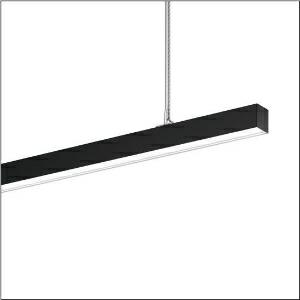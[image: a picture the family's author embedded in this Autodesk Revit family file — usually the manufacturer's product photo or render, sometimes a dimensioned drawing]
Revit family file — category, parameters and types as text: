
# Revit family: silica_21_51mx33dc3dbb
name_source: partatom
category: Lighting Fixtures
units: mm (PartAtom-declared; Revit-internal decimal feet)

## family parameters
Cut with Voids When Loaded = No
Host = Face
Light Source = No
Part Type = Normal
Room Calculation Point = No
Round Connector Dimension = Use Diameter
Shared = No

## types (1)
- --- (1 x LED, 14780 lm, 99.5 W, 3000K)
    Apparent Load = 100 VA
    CIE Flux Codes = 78 96 99 55 100
    Color Rendering = 80
    Color Temperature = 3000K
    Default Elevation = 1800 mm
    Description = Silica 21, office luminaire, primary optical cover: prismatic diffuser, of PMMA, CAT 2 (L<= 3000cd/m²), light emission: direct/indirect distribution, primary light characteristic: symmetric, installation type: suspended mounting, LED, rated luminous flux: 14.780lm, luminous efficacy: 149lm/W, light colour: 830, colour temperature: 3000K, control gear: DALI 2, with terminal, 3+2-pole, max. 2.5mm², mains connection: 220..240V, AC, 50/60Hz, rated input power: 99.5W, luminaire housing, of aluminium, matt jet black (RAL 9005), length: 3.004mm, width: 53mm, height: 53mm, protection rating (complete): IP20, insulation class (complete): insulation class I (protective earthing), certification: CE, permissible operating ambient temperature: 0..+35°C, standard: EN 50419, packaging unit: 1 piece
    Height = 53 mm
    Lamp = 1 x LED
    Lamp Light Flux = 14780 lm
    Lamp Power = 99.5 W
    Lamp count = 1
    Length = 3004 mm
    Luminous efficacy = 149 lm/W
    Manufacturer = Siteco
    ModVariant = No
    Model = 51MX33DC3DBB
    Mounting Place = Ceiling
    Mounting Type = Pendant
    Number of Poles = 1
    OnlyDefault = Yes
    Power Factor = 1
    Product Name = Silica 21
    Product group = office luminaire | ceiling pendant
    ProductGroupID = 903
    Protection Class = Protection class I
    Protection Degree = IP 20
    RLX_Detail_Level = 1
    RLX_Emergency_Light_Flux = 0 lm
    RLX_Emergency_Type = 0
    RLX_Emergency_Type_DB = No
    RlxData = <blob elided: 26205 chars, md5=c44d0621>
    Socket = socket
    Standby Power = 0 W
    System Light Flux = 14780 lm
    System Power = 100 W
    Type Comments = factory setting: luminous flux: 100 % | dim-lin: 254 | 345 mA
    Type Image = l_1335856.jpg
    URL = http://relux.com
    VarID = @adj_118795
    Voltage = 0 V
    Weight = 0.00 kg
    Width = 53 mm

## geometry (parser evidence)
native form markers: Blend x4, Sweep x17
no freeform markers — native parametric forms only
